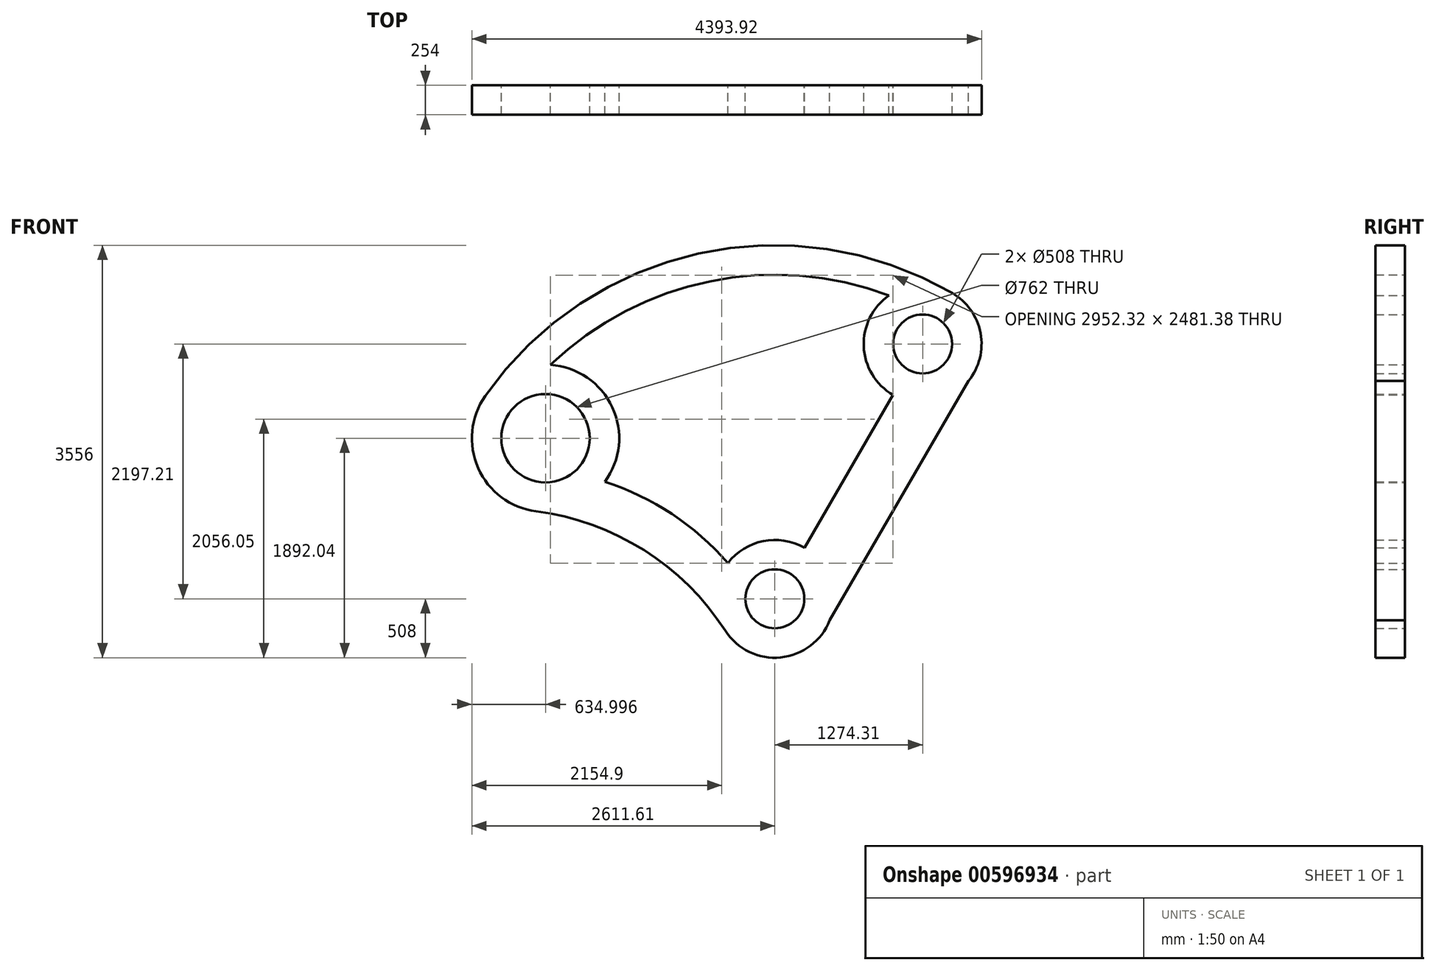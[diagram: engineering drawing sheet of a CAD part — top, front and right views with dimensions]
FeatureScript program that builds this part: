
annotation { "Feature Type Name" : "Feature", "Feature Type Description" : "" }
export const myFeature = defineFeature(function(context is Context, id is Id, definition is map)
    precondition{}
    {
        {
            var Q0;
            Q0=qCreatedBy(makeId("Front.planeOp"),FACE);
            var sketch = newSketch(context, id + "F0", { "sketchPlane" : qUnion([Q0])});
            skArc(sketch, "E0", {"start": v(-427.05, -275.12) * mm, "mid": v(50.46, -505.49) * mm, "end": v(473.01, -185.27) * mm});
            skCircle(sketch, "E1", {"center": v(0, 0) * mm, "radius": 254 * mm});
            skArc(sketch, "E2", {"start": v(984.84, 2614.67) * mm, "mid": v(766.72, 2176.71) * mm, "end": v(1019.45, 1757.77) * mm});
            skCircle(sketch, "E3", {"center": v(1274.3, 2197.21) * mm, "radius": 254 * mm});
            skLineSegment(sketch, "E4", {"start": v(1670.02, 1878.65) * mm, "end": v(395.7, -318.56) * mm});
            skArc(sketch, "E5", {"start": v(-2496.78, 1748.26) * mm, "mid": v(-2557.43, 1127.38) * mm, "end": v(-2057.52, 754.22) * mm});
            skCircle(sketch, "E6", {"center": v(-1976.61, 1384.04) * mm, "radius": 381 * mm});
            skArc(sketch, "E7", {"start": v(-427.05, -275.12) * mm, "mid": v(-1128.45, 419.87) * mm, "end": v(-2057.52, 754.22) * mm});
            skArc(sketch, "E8.trimOffspring", {"start": v(258.3, 437.43) * mm, "mid": v(-97.83, 498.5) * mm, "end": v(-404.46, 307.37) * mm});
            skPoint(sketch, "E9.centerSnap0", {"position": v(-1128.45, 419.87) * mm});
            skLineSegment(sketch, "E10", {"start": v(-1456.45, 1019.82) * mm, "end": v(-1415.97, 991.47) * mm});
            skArc(sketch, "E11.trimOffspring", {"start": v(-404.46, 307.37) * mm, "mid": v(-885.98, 731.5) * mm, "end": v(-1465.2, 1007.64) * mm});
            skArc(sketch, "E12", {"start": v(1529.17, 2636.65) * mm, "mid": v(-656.8, 2976.4) * mm, "end": v(-2496.78, 1748.26) * mm});
            skArc(sketch, "E13", {"start": v(984.84, 2614.67) * mm, "mid": v(-560.2, 2737.26) * mm, "end": v(-1932.87, 2017.53) * mm});
            skArc(sketch, "E14.trimOffspring", {"start": v(1670.02, 1878.65) * mm, "mid": v(1773.76, 2290.02) * mm, "end": v(1529.17, 2636.65) * mm});
            skArc(sketch, "E15.trimOffspring", {"start": v(-1465.2, 1007.64) * mm, "mid": v(-1400.4, 1650.88) * mm, "end": v(-1932.87, 2017.53) * mm});
            skLineSegment(sketch, "E16.trimOffspring", {"start": v(254.86, 439.44) * mm, "end": v(1019.45, 1757.77) * mm});
            skLineSegment(sketch, "E17.trimOffspring", {"start": v(-208.06, 145.69) * mm, "end": v(0, 0) * mm});
            skSolve(sketch);
        }
        {
            var Q0;
            {var subQ0=sQuery(id+"F0.wireOp",EDGE,"E4");var subQ1=sQuery(id+"F0.wireOp",EDGE,"E0");var subQ2=makeQuery(id+"F0.imprint","INTERSECT",VERTEX,{"disambiguationData":[OD(0.0)],"derivedFrom":[subQ1,subQ0]});Q0=makeQuery(id+"F0.imprint","IMPRINT",FACE,{"disambiguationData":[TD([[makeQuery(id+"F0.imprint","IMPRINT",EDGE,{"disambiguationData":[TD([[subQ2,1.0]])],"derivedFrom":subQ1}),1.0]])]});}
            var Q1;
            Q1=makeQuery(id+"F0.imprint","IMPRINT",FACE,{"disambiguationData":[TD([[makeQuery(id+"F0.imprint","IMPRINT",EDGE,{"derivedFrom":sQuery(id+"F0.wireOp",EDGE,"E1")}),-1.0]])]});
            extrude(context, id + "F1", {"entities" : qUnion([Q0, Q1]), "depth" : 254 * mm, "offsetDistance" : 25.4 * mm});
        }
    });
